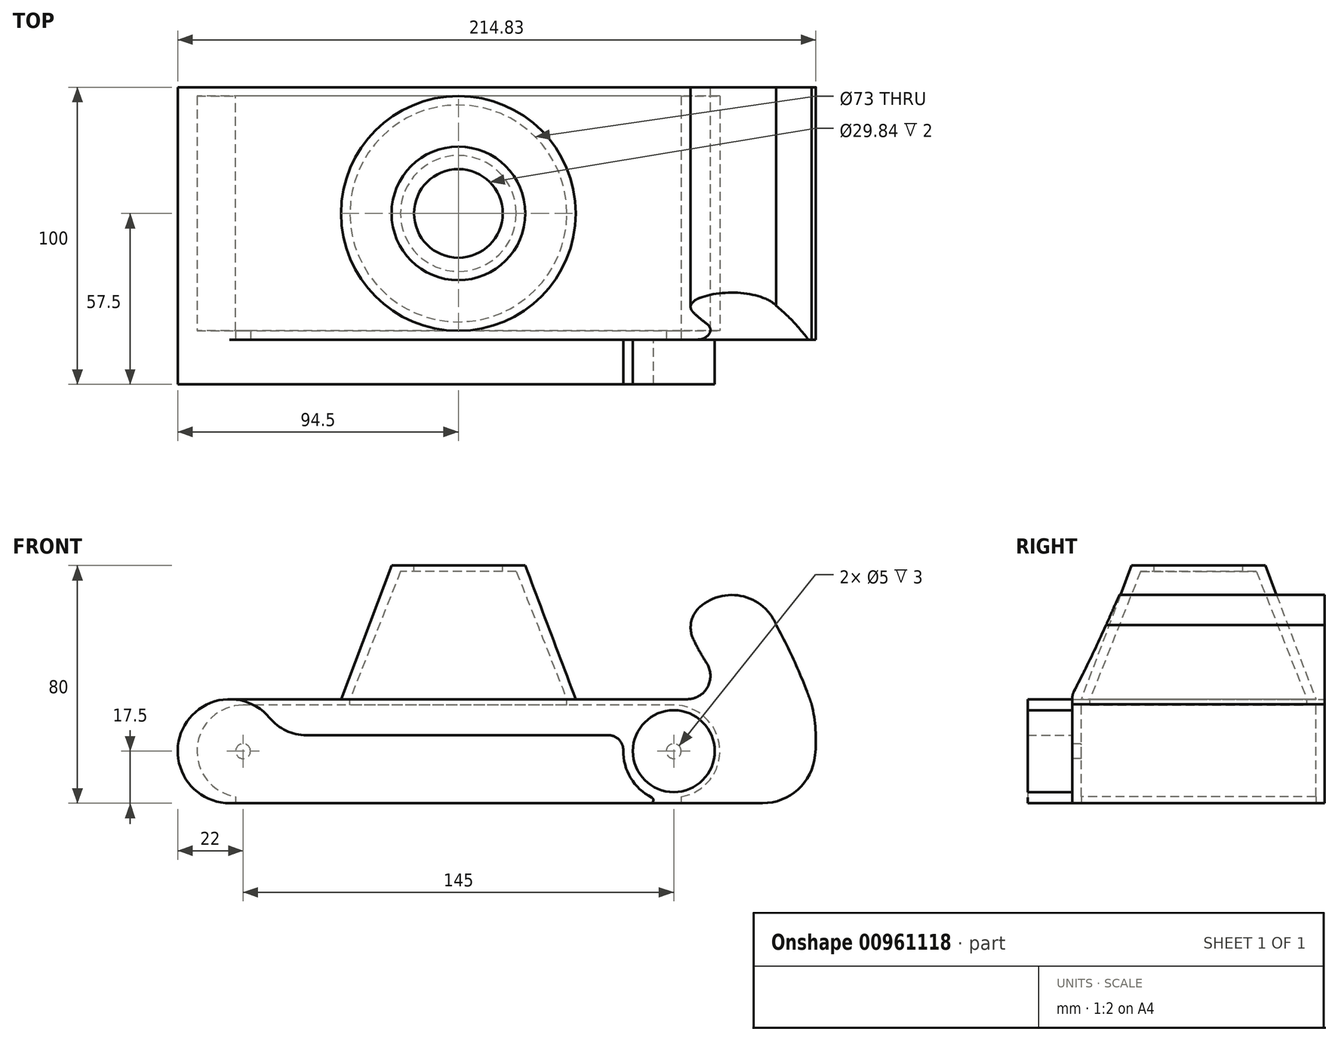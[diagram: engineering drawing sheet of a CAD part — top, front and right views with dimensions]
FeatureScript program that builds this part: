
annotation { "Feature Type Name" : "Feature", "Feature Type Description" : "" }
export const myFeature = defineFeature(function(context is Context, id is Id, definition is map)
    precondition{}
    {
        {
            var Q0;
            Q0=qCreatedBy(makeId("Front.planeOp"),FACE);
            var sketch = newSketch(context, id + "F0", { "sketchPlane" : qUnion([Q0])});
            skLineSegment(sketch, "E0.bottom", {"start": v(77, 17.5) * mm, "end": v(-77, 17.5) * mm, "construction": true});
            skLineSegment(sketch, "E0.top", {"start": v(77, -17.5) * mm, "end": v(-77, -17.5) * mm, "construction": true});
            skLineSegment(sketch, "E0.left", {"start": v(77, 17.5) * mm, "end": v(77, -17.5) * mm, "construction": true});
            skLineSegment(sketch, "E0.right", {"start": v(-77, 17.5) * mm, "end": v(-77, -17.5) * mm, "construction": true});
            skPoint(sketch, "E0.middle", {"position": v(0, 0) * mm});
            skArc(sketch, "E1", {"start": v(-77, 17.5) * mm, "mid": v(-94.5, 0) * mm, "end": v(-77, -17.5) * mm});
            skLineSegment(sketch, "E2", {"start": v(77, 17.5) * mm, "end": v(77, 42.5) * mm, "construction": true});
            skLineSegment(sketch, "E3", {"start": v(77, 42.5) * mm, "end": v(107, 42.5) * mm, "construction": true});
            skLineSegment(sketch, "E4", {"start": v(107, 42.5) * mm, "end": v(107, -17.5) * mm, "construction": true});
            skLineSegment(sketch, "E5", {"start": v(107, -17.5) * mm, "end": v(77, -17.5) * mm, "construction": true});
            skLineSegment(sketch, "E6.bottom", {"start": v(52.5, 0) * mm, "end": v(-52.5, 0) * mm, "construction": true});
            skLineSegment(sketch, "E6.top", {"start": v(52.5, 0) * mm, "end": v(-52.5, 0) * mm, "construction": true});
            skLineSegment(sketch, "E6.left", {"start": v(52.5, 0) * mm, "end": v(52.5, 0) * mm});
            skLineSegment(sketch, "E6.right", {"start": v(-52.5, 0) * mm, "end": v(-52.5, 0) * mm});
            skCircle(sketch, "E7", {"center": v(52.5, 0) * mm, "radius": 1.5 * mm, "construction": true});
            skCircle(sketch, "E8", {"center": v(-52.5, 0) * mm, "radius": 1.5 * mm, "construction": true});
            skLineSegment(sketch, "E9", {"start": v(107, 15.8) * mm, "end": v(118.94, 15.8) * mm, "construction": true});
            skArc(sketch, "E10", {"start": v(107, 42.5) * mm, "mid": v(92, 52.6) * mm, "end": v(77, 42.5) * mm});
            skArc(sketch, "E11", {"start": v(118.94, 15.8) * mm, "mid": v(113.49, 29.38) * mm, "end": v(107, 42.5) * mm});
            skArc(sketch, "E12", {"start": v(115.95, -17.5) * mm, "mid": v(120.12, -1.1) * mm, "end": v(118.94, 15.8) * mm});
            skLineSegment(sketch, "E13", {"start": v(115.95, -17.5) * mm, "end": v(107, -17.5) * mm});
            skLineSegment(sketch, "E14", {"start": v(53.68, 17.5) * mm, "end": v(-77, 17.5) * mm});
            skLineSegment(sketch, "E15", {"start": v(-77, -17.5) * mm, "end": v(107, -17.5) * mm});
            skArc(sketch, "E16", {"start": v(77, 42.5) * mm, "mid": v(79.98, 35.88) * mm, "end": v(83.61, 29.59) * mm});
            skArc(sketch, "E17", {"start": v(77, 17.5) * mm, "mid": v(83.89, 21.58) * mm, "end": v(83.61, 29.59) * mm});
            skLineSegment(sketch, "E18", {"start": v(77, 17.5) * mm, "end": v(53.68, 17.5) * mm});
            skSolve(sketch);
        }
        {
            var Q0;
            Q0=qSketchRegion(id+"F0",true);
            extrude(context, id + "F1", {"entities" : qUnion([Q0]), "depth" : 85 * mm, "offsetDistance" : 25 * mm});
        }
        {
            var Q0;
            Q0=makeQuery(id+"F1.opExtrude","CAP_FACE",FACE,{"disambiguationData":[OSD([sQuery(id+"F0.wireOp",EDGE,"E1"),sQuery(id+"F0.wireOp",EDGE,"v8Q2QpjE-PcgM-wgtQ-MVAr-s5shNDQ3cLfB"),sQuery(id+"F0.wireOp",EDGE,"E10"),sQuery(id+"F0.wireOp",EDGE,"E11"),sQuery(id+"F0.wireOp",EDGE,"E12"),sQuery(id+"F0.wireOp",EDGE,"E13"),sQuery(id+"F0.wireOp",EDGE,"E14"),sQuery(id+"F0.wireOp",EDGE,"E15")])],"isStart":false});
            var sketch = newSketch(context, id + "F2", { "sketchPlane" : qUnion([Q0])});
            skLineSegment(sketch, "E19.bottom", {"start": v(72.5, 15.5) * mm, "end": v(-72.5, 15.5) * mm});
            skLineSegment(sketch, "E19.top", {"start": v(72.5, -15.5) * mm, "end": v(-72.5, -15.5) * mm});
            skLineSegment(sketch, "E19.left", {"start": v(72.5, 15.5) * mm, "end": v(72.5, -15.5) * mm});
            skLineSegment(sketch, "E19.right", {"start": v(-72.5, 15.5) * mm, "end": v(-72.5, -15.5) * mm});
            skPoint(sketch, "E19.middle", {"position": v(0, 0) * mm});
            skArc(sketch, "E20", {"start": v(-72.5, 15.5) * mm, "mid": v(-88, 0) * mm, "end": v(-72.5, -15.5) * mm});
            skArc(sketch, "E21", {"start": v(72.5, -15.5) * mm, "mid": v(88, 0) * mm, "end": v(72.5, 15.5) * mm});
            skSolve(sketch);
        }
        {
            var Q0;
            Q0=qSketchRegion(id+"F2",true);
            extrude(context, id + "F3", {"entities" : qUnion([Q0]), "operationType" : NewBodyOperationType.REMOVE, "oppositeDirection" : true, "depth" : 82 * mm, "offsetDistance" : 25 * mm});
        }
        {
            var Q0;
            Q0=makeQuery(id+"F1.opExtrude","CAP_FACE",FACE,{"disambiguationData":[OSD([sQuery(id+"F0.wireOp",EDGE,"E1"),sQuery(id+"F0.wireOp",EDGE,"v8Q2QpjE-PcgM-wgtQ-MVAr-s5shNDQ3cLfB"),sQuery(id+"F0.wireOp",EDGE,"E10"),sQuery(id+"F0.wireOp",EDGE,"E11"),sQuery(id+"F0.wireOp",EDGE,"E12"),sQuery(id+"F0.wireOp",EDGE,"E13"),sQuery(id+"F0.wireOp",EDGE,"E14"),sQuery(id+"F0.wireOp",EDGE,"E15")])],"isStart":false});
            var sketch = newSketch(context, id + "F4", { "sketchPlane" : qUnion([Q0])});
            skLineSegment(sketch, "E22", {"start": v(-89.82, 7.1) * mm, "end": v(-80.33, 15.81) * mm});
            skLineSegment(sketch, "E23", {"start": v(-80.33, 15.81) * mm, "end": v(-69.61, 16.64) * mm});
            skLineSegment(sketch, "E24", {"start": v(-69.61, 16.64) * mm, "end": v(67.79, 16.64) * mm});
            skLineSegment(sketch, "E25", {"start": v(67.79, 16.64) * mm, "end": v(83.17, 16.64) * mm});
            skLineSegment(sketch, "E26", {"start": v(83.17, 16.64) * mm, "end": v(95.83, 5.41) * mm});
            skLineSegment(sketch, "E27", {"start": v(95.83, 5.41) * mm, "end": v(93.18, -10.93) * mm});
            skLineSegment(sketch, "E28", {"start": v(93.18, -10.93) * mm, "end": v(83.17, -15.5) * mm});
            skLineSegment(sketch, "E29", {"start": v(83.17, -15.5) * mm, "end": v(74.39, -16.42) * mm});
            skLineSegment(sketch, "E30", {"start": v(74.39, -16.42) * mm, "end": v(-77, -16.42) * mm});
            skLineSegment(sketch, "E31", {"start": v(-77, -16.42) * mm, "end": v(-85, -14.22) * mm});
            skLineSegment(sketch, "E32", {"start": v(-85, -14.22) * mm, "end": v(-88.28, -7.94) * mm});
            skLineSegment(sketch, "E33", {"start": v(-88.28, -7.94) * mm, "end": v(-91.01, 2.98) * mm});
            skLineSegment(sketch, "E34", {"start": v(-91.01, 2.98) * mm, "end": v(-89.82, 7.1) * mm});
            skSolve(sketch);
        }
        {
            var Q0;
            Q0=qSketchRegion(id+"F4",true);
            extrude(context, id + "F5", {"entities" : qUnion([Q0]), "operationType" : NewBodyOperationType.ADD, "oppositeDirection" : true, "depth" : 3 * mm, "offsetDistance" : 25 * mm});
        }
        {
            var Q0;
            Q0=makeQuery(id+"F1.opExtrude","SWEPT_FACE",FACE,{"disambiguationData":[OSD([sQuery(id+"F0.wireOp",EDGE,"E14")])]});
            var sketch = newSketch(context, id + "F6", { "sketchPlane" : qUnion([Q0])});
            skLineSegment(sketch, "E35", {"start": v(0, 0) * mm, "end": v(0, -85) * mm, "construction": true});
            skCircle(sketch, "E36", {"center": v(0, -42.5) * mm, "radius": 36.5 * mm});
            skSolve(sketch);
        }
        {
            var Q0;
            Q0=qSketchRegion(id+"F6",true);
            extrude(context, id + "F7", {"entities" : qUnion([Q0]), "operationType" : NewBodyOperationType.REMOVE, "oppositeDirection" : true, "depth" : 25 * mm, "offsetDistance" : 25 * mm});
        }
        {
            var Q0;
            Q0=makeQuery(id+"F1.opExtrude","SWEPT_FACE",FACE,{"disambiguationData":[OSD([sQuery(id+"F0.wireOp",EDGE,"E13"),sQuery(id+"F0.wireOp",EDGE,"E15")])]});
            var sketch = newSketch(context, id + "F8", { "sketchPlane" : qUnion([Q0])});
            skLineSegment(sketch, "E37", {"start": v(0, 0) * mm, "end": v(0, 85) * mm, "construction": true});
            skLineSegment(sketch, "E38.bottom", {"start": v(75, 82) * mm, "end": v(-75, 82) * mm});
            skLineSegment(sketch, "E38.top", {"start": v(75, 3) * mm, "end": v(-75, 3) * mm});
            skLineSegment(sketch, "E38.left", {"start": v(75, 82) * mm, "end": v(75, 3) * mm});
            skLineSegment(sketch, "E38.right", {"start": v(-75, 82) * mm, "end": v(-75, 3) * mm});
            skPoint(sketch, "E38.middle", {"position": v(0, 42.5) * mm});
            skSolve(sketch);
        }
        {
            var Q0;
            Q0=qSketchRegion(id+"F8",true);
            extrude(context, id + "F9", {"entities" : qUnion([Q0]), "operationType" : NewBodyOperationType.REMOVE, "oppositeDirection" : true, "depth" : 25 * mm, "offsetDistance" : 25 * mm});
        }
        {
            var Q0;
            Q0=makeQuery(id+"F1.opExtrude","SWEPT_FACE",FACE,{"disambiguationData":[OSD([sQuery(id+"F0.wireOp",EDGE,"E14")])]});
            cPlane(context, id + "F10", {"entities" : qUnion([Q0]), "cplaneType" : CPlaneType.OFFSET, "offset" : 45 * mm, "width" : 150 * mm, "height" : 150 * mm});
        }
        {
            var Q0;
            Q0=qCreatedBy(id+"F10.planeOp",FACE);
            var sketch = newSketch(context, id + "F11", { "sketchPlane" : qUnion([Q0])});
            skLineSegment(sketch, "E39", {"start": v(0, 0) * mm, "end": v(0, -85) * mm, "construction": true});
            skCircle(sketch, "E40", {"center": v(0, -42.5) * mm, "radius": 22.5 * mm});
            skSolve(sketch);
        }
        {
            var Q0;
            Q0=makeQuery(id+"F1.opExtrude","SWEPT_FACE",FACE,{"disambiguationData":[OSD([sQuery(id+"F0.wireOp",EDGE,"E14")])]});
            var sketch = newSketch(context, id + "F12", { "sketchPlane" : qUnion([Q0])});
            skLineSegment(sketch, "E41", {"start": v(0, 0) * mm, "end": v(0, -85) * mm, "construction": true});
            skCircle(sketch, "E42", {"center": v(0, -42.5) * mm, "radius": 39.5 * mm});
            skSolve(sketch);
        }
        {
            var Q1;
            Q1=qSketchRegion(id+"F12",true);
            var Q2;
            Q2=qSketchRegion(id+"F11",true);
            loft(context, id + "F13", {"operationType" : NewBodyOperationType.ADD, "sheetProfilesArray" : [{ "sheetProfileEntities" : qUnion([Q1]) }, { "sheetProfileEntities" : qUnion([Q2]) }]});
        }
        {
            var Q0;
            Q0=qCreatedBy(id+"F10.planeOp",FACE);
            cPlane(context, id + "F14", {"entities" : qUnion([Q0]), "cplaneType" : CPlaneType.OFFSET, "offset" : 2 * mm, "oppositeDirection" : true, "width" : 150 * mm, "height" : 150 * mm});
        }
        {
            var Q0;
            Q0=qCreatedBy(id+"F14.planeOp",FACE);
            var sketch = newSketch(context, id + "F15", { "sketchPlane" : qUnion([Q0])});
            skLineSegment(sketch, "E43", {"start": v(0, 0) * mm, "end": v(0, -85) * mm, "construction": true});
            skCircle(sketch, "E44", {"center": v(0, -42.5) * mm, "radius": 19.5 * mm});
            skSolve(sketch);
        }
        {
            var Q0;
            {var subQ0=makeQuery(id+"F12.imprint","IMPRINT",EDGE,{"derivedFrom":makeQuery(id+"F7.boolean.opBoolean","COPY",EDGE,{"derivedFrom":makeQuery(id+"F7.opExtrude","CAP_EDGE",EDGE,{"disambiguationData":[OSD([sQuery(id+"F6.wireOp",EDGE,"E36")])],"isStart":true})})});Q0=makeQuery(id+"F13.opLoft","CAP_FACE",FACE,{"disambiguationData":[OSD([makeQuery(id+"F12.imprint","IMPRINT",FACE,{"disambiguationData":[TD([[subQ0,1.0]])]}),makeQuery(id+"F12.imprint","IMPRINT",FACE,{"disambiguationData":[TD([[makeQuery(id+"F12.imprint","IMPRINT",EDGE,{"derivedFrom":sQuery(id+"F12.wireOp",EDGE,"E42")}),1.0]])]})])],"isStart":true});}
            var sketch = newSketch(context, id + "F16", { "sketchPlane" : qUnion([Q0])});
            skCircle(sketch, "E45", {"center": v(0, 42.5) * mm, "radius": 36.5 * mm});
            skSolve(sketch);
        }
        {
            var Q1;
            Q1=qSketchRegion(id+"F15",true);
            var Q2;
            Q2=qSketchRegion(id+"F16",true);
            loft(context, id + "F17", {"operationType" : NewBodyOperationType.REMOVE, "sheetProfilesArray" : [{ "sheetProfileEntities" : qUnion([Q1]) }, { "sheetProfileEntities" : qUnion([Q2]) }]});
        }
        {
            var Q0;
            Q0=makeQuery(id+"F13.opLoft","CAP_FACE",FACE,{"disambiguationData":[OSD([makeQuery(id+"F11.imprint","IMPRINT",FACE,{"disambiguationData":[TD([[makeQuery(id+"F11.imprint","IMPRINT",EDGE,{"derivedFrom":sQuery(id+"F11.wireOp",EDGE,"E40")}),1.0]])]})])],"isStart":true});
            var sketch = newSketch(context, id + "F18", { "sketchPlane" : qUnion([Q0])});
            skCircle(sketch, "E46", {"center": v(0, -42.5) * mm, "radius": 14.92 * mm});
            skSolve(sketch);
        }
        {
            var Q0;
            Q0=qSketchRegion(id+"F18",true);
            extrude(context, id + "F19", {"entities" : qUnion([Q0]), "operationType" : NewBodyOperationType.REMOVE, "oppositeDirection" : true, "depth" : 25 * mm, "offsetDistance" : 25 * mm});
        }
        {
            var Q0;
            Q0=makeQuery(id+"F1.opExtrude","SWEPT_EDGE",EDGE,{"disambiguationData":[OSD([sQuery(id+"F0.wireOp",EDGE,"E12"),sQuery(id+"F0.wireOp",EDGE,"E13")])]});
            fillet(context, id + "F20", {"entities" : qUnion([Q0]), "radius" : 17.8 * mm, "tangentPropagation" : true, "allowEdgeOverflow" : false});
        }
        {
            var Q0;
            Q0=makeQuery(id+"F1.opExtrude","SWEPT_EDGE",EDGE,{"disambiguationData":[OSD([sQuery(id+"F0.wireOp",EDGE,"E10"),sQuery(id+"F0.wireOp",EDGE,"E16")])]});
            fillet(context, id + "F21", {"entities" : qUnion([Q0]), "radius" : 9.17 * mm, "tangentPropagation" : true, "allowEdgeOverflow" : false});
        }
        {
            var Q0;
            Q0=qCreatedBy(makeId("Right.planeOp"),FACE);
            cPlane(context, id + "F22", {"entities" : qUnion([Q0]), "cplaneType" : CPlaneType.OFFSET, "offset" : 122 * mm, "width" : 150 * mm, "height" : 150 * mm});
        }
        {
            var Q0;
            Q0=qCreatedBy(id+"F22.planeOp",FACE);
            var sketch = newSketch(context, id + "F23", { "sketchPlane" : qUnion([Q0])});
            skLineSegment(sketch, "E47", {"start": v(-68.17, 54.85) * mm, "end": v(-80.75, 26) * mm});
            skLineSegment(sketch, "E48", {"start": v(-80.75, 26) * mm, "end": v(-85.65, 18.18) * mm});
            skLineSegment(sketch, "E49", {"start": v(-85.65, 18.18) * mm, "end": v(-88.56, 59.22) * mm});
            skLineSegment(sketch, "E50", {"start": v(-88.56, 59.22) * mm, "end": v(-68.17, 54.85) * mm});
            skSolve(sketch);
        }
        {
            var Q0;
            Q0 = qSketchRegion(id + "F23", true);
            extrude(context, id + "F24", {"entities" : qUnion([Q0]), "operationType" : NewBodyOperationType.REMOVE, "oppositeDirection" : true, "depth" : 48.2 * mm, "offsetDistance" : 25 * mm});
        }
        {
            var Q0;
            Q0=makeQuery(id+"F24.boolean.opBoolean","INTERSECT",EDGE,{"derivedFrom":[makeQuery(id+"F5.boolean.opBoolean","MERGE",FACE,{"derivedFrom":[makeQuery(id+"F1.opExtrude","CAP_FACE",FACE,{"disambiguationData":[OSD([sQuery(id+"F0.wireOp",EDGE,"E1"),sQuery(id+"F0.wireOp",EDGE,"E10"),sQuery(id+"F0.wireOp",EDGE,"E11"),sQuery(id+"F0.wireOp",EDGE,"E12"),sQuery(id+"F0.wireOp",EDGE,"E13"),sQuery(id+"F0.wireOp",EDGE,"E14"),sQuery(id+"F0.wireOp",EDGE,"E15"),sQuery(id+"F0.wireOp",EDGE,"E16"),sQuery(id+"F0.wireOp",EDGE,"E17"),sQuery(id+"F0.wireOp",EDGE,"E18")])],"isStart":false}),makeQuery(id+"F5.opExtrude","CAP_FACE",FACE,{"disambiguationData":[OSD([sQuery(id+"F4.wireOp",EDGE,"E22"),sQuery(id+"F4.wireOp",EDGE,"E23"),sQuery(id+"F4.wireOp",EDGE,"E24"),sQuery(id+"F4.wireOp",EDGE,"E25"),sQuery(id+"F4.wireOp",EDGE,"E26"),sQuery(id+"F4.wireOp",EDGE,"E27"),sQuery(id+"F4.wireOp",EDGE,"E28"),sQuery(id+"F4.wireOp",EDGE,"E29"),sQuery(id+"F4.wireOp",EDGE,"E30"),sQuery(id+"F4.wireOp",EDGE,"E31"),sQuery(id+"F4.wireOp",EDGE,"E32"),sQuery(id+"F4.wireOp",EDGE,"E33"),sQuery(id+"F4.wireOp",EDGE,"E34")])],"isStart":true})]}),makeQuery(id+"F24.opExtrude","SWEPT_FACE",FACE,{"disambiguationData":[OSD([sQuery(id+"F23.wireOp",EDGE,"E48")])]})]});
            fillet(context, id + "F25", {"entities" : qUnion([Q0]), "radius" : 4.93 * mm, "tangentPropagation" : true, "allowEdgeOverflow" : false});
        }
        {
            var Q0;
            Q0=makeQuery(id+"F24.boolean.opBoolean","COPY",EDGE,{"derivedFrom":makeQuery(id+"F24.opExtrude","SWEPT_EDGE",EDGE,{"disambiguationData":[OSD([sQuery(id+"F23.wireOp",EDGE,"E47"),sQuery(id+"F23.wireOp",EDGE,"E48")])]})});
            fillet(context, id + "F26", {"entities" : qUnion([Q0]), "radius" : 466.4 * mm, "tangentPropagation" : true, "allowEdgeOverflow" : false});
        }
        {
            var Q0;
            Q0=makeQuery(id+"F5.boolean.opBoolean","MERGE",FACE,{"derivedFrom":[makeQuery(id+"F1.opExtrude","CAP_FACE",FACE,{"disambiguationData":[OSD([sQuery(id+"F0.wireOp",EDGE,"E1"),sQuery(id+"F0.wireOp",EDGE,"E10"),sQuery(id+"F0.wireOp",EDGE,"E11"),sQuery(id+"F0.wireOp",EDGE,"E12"),sQuery(id+"F0.wireOp",EDGE,"E13"),sQuery(id+"F0.wireOp",EDGE,"E14"),sQuery(id+"F0.wireOp",EDGE,"E15"),sQuery(id+"F0.wireOp",EDGE,"E16"),sQuery(id+"F0.wireOp",EDGE,"E17"),sQuery(id+"F0.wireOp",EDGE,"E18")])],"isStart":false}),makeQuery(id+"F5.opExtrude","CAP_FACE",FACE,{"disambiguationData":[OSD([sQuery(id+"F4.wireOp",EDGE,"E22"),sQuery(id+"F4.wireOp",EDGE,"E23"),sQuery(id+"F4.wireOp",EDGE,"E24"),sQuery(id+"F4.wireOp",EDGE,"E25"),sQuery(id+"F4.wireOp",EDGE,"E26"),sQuery(id+"F4.wireOp",EDGE,"E27"),sQuery(id+"F4.wireOp",EDGE,"E28"),sQuery(id+"F4.wireOp",EDGE,"E29"),sQuery(id+"F4.wireOp",EDGE,"E30"),sQuery(id+"F4.wireOp",EDGE,"E31"),sQuery(id+"F4.wireOp",EDGE,"E32"),sQuery(id+"F4.wireOp",EDGE,"E33"),sQuery(id+"F4.wireOp",EDGE,"E34")])],"isStart":true})]});
            var sketch = newSketch(context, id + "F27", { "sketchPlane" : qUnion([Q0])});
            skLineSegment(sketch, "E51.bottom", {"start": v(72.5, 0) * mm, "end": v(-72.5, 0) * mm, "construction": true});
            skLineSegment(sketch, "E51.top", {"start": v(72.5, 0) * mm, "end": v(-72.5, 0) * mm, "construction": true});
            skLineSegment(sketch, "E51.left", {"start": v(72.5, 0) * mm, "end": v(72.5, 0) * mm});
            skLineSegment(sketch, "E51.right", {"start": v(-72.5, 0) * mm, "end": v(-72.5, 0) * mm});
            skPoint(sketch, "E51.middle", {"position": v(0, 0) * mm});
            skCircle(sketch, "E52", {"center": v(72.5, 0) * mm, "radius": 2.5 * mm});
            skCircle(sketch, "E53", {"center": v(-72.5, 0) * mm, "radius": 2.5 * mm});
            skSolve(sketch);
        }
        {
            var Q0;
            Q0 = qSketchRegion(id + "F27", true);
            extrude(context, id + "F28", {"entities" : qUnion([Q0]), "operationType" : NewBodyOperationType.REMOVE, "oppositeDirection" : true, "depth" : 25 * mm, "offsetDistance" : 25 * mm});
        }
        {
            var Q0;
            Q0=makeQuery(id+"F5.boolean.opBoolean","MERGE",FACE,{"derivedFrom":[makeQuery(id+"F1.opExtrude","CAP_FACE",FACE,{"disambiguationData":[OSD([sQuery(id+"F0.wireOp",EDGE,"E1"),sQuery(id+"F0.wireOp",EDGE,"E10"),sQuery(id+"F0.wireOp",EDGE,"E11"),sQuery(id+"F0.wireOp",EDGE,"E12"),sQuery(id+"F0.wireOp",EDGE,"E13"),sQuery(id+"F0.wireOp",EDGE,"E14"),sQuery(id+"F0.wireOp",EDGE,"E15"),sQuery(id+"F0.wireOp",EDGE,"E16"),sQuery(id+"F0.wireOp",EDGE,"E17"),sQuery(id+"F0.wireOp",EDGE,"E18")])],"isStart":false}),makeQuery(id+"F5.opExtrude","CAP_FACE",FACE,{"disambiguationData":[OSD([sQuery(id+"F4.wireOp",EDGE,"E22"),sQuery(id+"F4.wireOp",EDGE,"E23"),sQuery(id+"F4.wireOp",EDGE,"E24"),sQuery(id+"F4.wireOp",EDGE,"E25"),sQuery(id+"F4.wireOp",EDGE,"E26"),sQuery(id+"F4.wireOp",EDGE,"E27"),sQuery(id+"F4.wireOp",EDGE,"E28"),sQuery(id+"F4.wireOp",EDGE,"E29"),sQuery(id+"F4.wireOp",EDGE,"E30"),sQuery(id+"F4.wireOp",EDGE,"E31"),sQuery(id+"F4.wireOp",EDGE,"E32"),sQuery(id+"F4.wireOp",EDGE,"E33"),sQuery(id+"F4.wireOp",EDGE,"E34")])],"isStart":true})]});
            var sketch = newSketch(context, id + "F29", { "sketchPlane" : qUnion([Q0])});
            skArc(sketch, "E54", {"start": v(-77, 17.5) * mm, "mid": v(-94.5, 0) * mm, "end": v(-77, -17.5) * mm});
            skLineSegment(sketch, "E55", {"start": v(-77, -17.5) * mm, "end": v(73, -17.5) * mm});
            skLineSegment(sketch, "E56", {"start": v(-60.35, 5.4) * mm, "end": v(56.35, 5.4) * mm});
            skArc(sketch, "E57", {"start": v(56.35, 5.4) * mm, "mid": v(58.84, -10.29) * mm, "end": v(73, -17.5) * mm});
            skArc(sketch, "E58", {"start": v(-60.35, 5.4) * mm, "mid": v(-66.71, 14.16) * mm, "end": v(-77, 17.5) * mm});
            skSolve(sketch);
        }
        {
            var Q0;
            Q0 = qSketchRegion(id + "F29", true);
            extrude(context, id + "F30", {"entities" : qUnion([Q0]), "operationType" : NewBodyOperationType.ADD, "depth" : 15 * mm, "offsetDistance" : 25 * mm});
        }
        {
            var Q0;
            Q0=makeQuery(id+"F30.opExtrude","SWEPT_EDGE",EDGE,{"disambiguationData":[OSD([sQuery(id+"F29.wireOp",EDGE,"E56"),sQuery(id+"F29.wireOp",EDGE,"E58")])]});
            fillet(context, id + "F31", {"entities" : qUnion([Q0]), "radius" : 16.09 * mm, "tangentPropagation" : true, "allowEdgeOverflow" : false});
        }
        {
            var Q0;
            Q0=makeQuery(id+"F30.opExtrude","SWEPT_EDGE",EDGE,{"disambiguationData":[OSD([sQuery(id+"F0.wireOp",EDGE,"E13"),sQuery(id+"F0.wireOp",EDGE,"E15"),sQuery(id+"F29.wireOp",EDGE,"E55"),sQuery(id+"F29.wireOp",EDGE,"E57")])]});
            fillet(context, id + "F32", {"entities" : qUnion([Q0]), "radius" : 1 * mm, "tangentPropagation" : true, "allowEdgeOverflow" : false});
        }
        {
            var Q0;
            Q0=makeQuery(id+"F30.opExtrude","SWEPT_EDGE",EDGE,{"disambiguationData":[OSD([sQuery(id+"F29.wireOp",EDGE,"E56"),sQuery(id+"F29.wireOp",EDGE,"E57")])]});
            fillet(context, id + "F33", {"entities" : qUnion([Q0]), "radius" : 5 * mm, "tangentPropagation" : true, "allowEdgeOverflow" : false});
        }
        {
            var Q0;
            Q0=makeQuery(id+"F5.boolean.opBoolean","MERGE",FACE,{"derivedFrom":[makeQuery(id+"F1.opExtrude","CAP_FACE",FACE,{"disambiguationData":[OSD([sQuery(id+"F0.wireOp",EDGE,"E1"),sQuery(id+"F0.wireOp",EDGE,"E10"),sQuery(id+"F0.wireOp",EDGE,"E11"),sQuery(id+"F0.wireOp",EDGE,"E12"),sQuery(id+"F0.wireOp",EDGE,"E13"),sQuery(id+"F0.wireOp",EDGE,"E14"),sQuery(id+"F0.wireOp",EDGE,"E15"),sQuery(id+"F0.wireOp",EDGE,"E16"),sQuery(id+"F0.wireOp",EDGE,"E17"),sQuery(id+"F0.wireOp",EDGE,"E18")])],"isStart":false}),makeQuery(id+"F5.opExtrude","CAP_FACE",FACE,{"disambiguationData":[OSD([sQuery(id+"F4.wireOp",EDGE,"E22"),sQuery(id+"F4.wireOp",EDGE,"E23"),sQuery(id+"F4.wireOp",EDGE,"E24"),sQuery(id+"F4.wireOp",EDGE,"E25"),sQuery(id+"F4.wireOp",EDGE,"E26"),sQuery(id+"F4.wireOp",EDGE,"E27"),sQuery(id+"F4.wireOp",EDGE,"E28"),sQuery(id+"F4.wireOp",EDGE,"E29"),sQuery(id+"F4.wireOp",EDGE,"E30"),sQuery(id+"F4.wireOp",EDGE,"E31"),sQuery(id+"F4.wireOp",EDGE,"E32"),sQuery(id+"F4.wireOp",EDGE,"E33"),sQuery(id+"F4.wireOp",EDGE,"E34")])],"isStart":true})]});
            var sketch = newSketch(context, id + "F34", { "sketchPlane" : qUnion([Q0])});
            skCircle(sketch, "E59", {"center": v(72.5, 0) * mm, "radius": 13.78 * mm});
            skSolve(sketch);
        }
        {
            var Q0;
            Q0 = qSketchRegion(id + "F34", true);
            extrude(context, id + "F35", {"entities" : qUnion([Q0]), "operationType" : NewBodyOperationType.ADD, "depth" : 15 * mm, "offsetDistance" : 25 * mm});
        }
    });
